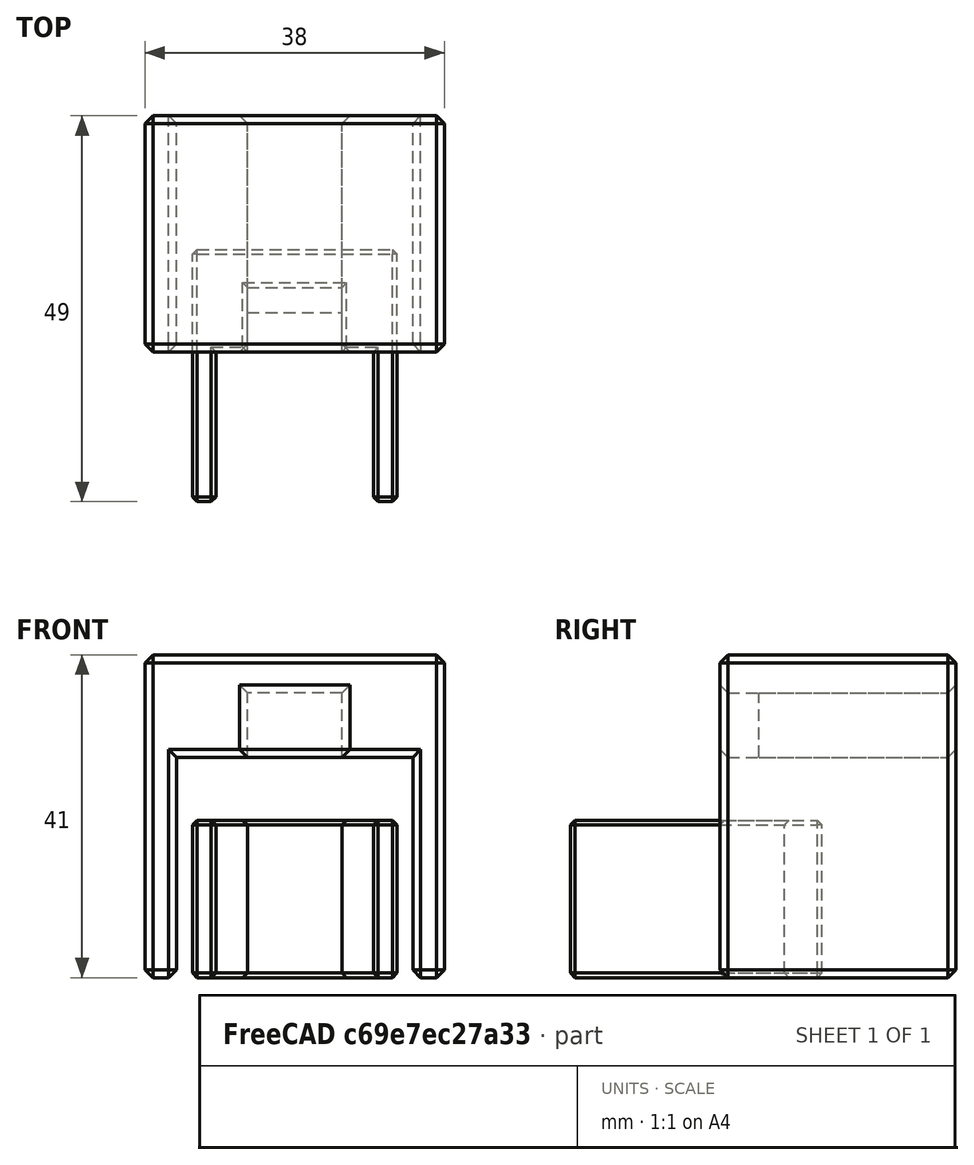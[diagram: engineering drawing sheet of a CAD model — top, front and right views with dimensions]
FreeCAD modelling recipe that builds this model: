
FCSTD DOCUMENT  (FreeCAD 0.18R16146 (Git))
Label: rail-aliner
License: All rights reserved
LicenseURL: http://en.wikipedia.org/wiki/All_rights_reserved
objects: Part::Box×7, Part::MultiFuse×3, Part::Chamfer×3, Part::Cut×2, Part::Feature×1
note: 16 computed .brp shape members not serialized (recipe doc carries the construction recipe); baked Part::Feature solids carry a one-line shape summary decoded from their .brp

FEATURE [Part::Box] Box003  label="Cube003"
  AttacherType = Attacher::AttachEngine3D
  Height = 10.2
  Length = 14.2
  Placement = pos=(-7.1,0,28) rot=(0,0,1;0rad)
  Width = 5
FEATURE [Part::Box] Box005  label="Cube005"
  AttacherType = Attacher::AttachEngine3D
  Height = 28
  Length = 30
  Placement = pos=(-15,0,0) rot=(0,0,1;0rad)
  Width = 30
FEATURE [Part::Box] Box006  label="Cube006"
  AttacherType = Attacher::AttachEngine3D
  Height = 8.2
  Length = 12
  Placement = pos=(-6,0,28) rot=(0,0,1;0rad)
  Width = 30
FEATURE [Part::Box] Box007  label="Cube007"
  AttacherType = Attacher::AttachEngine3D
  Height = 41
  Length = 38
  Placement = pos=(-19,0,0) rot=(0,0,1;0rad)
  Width = 30
FEATURE [Part::Box] Box  label="Cube"
  AttacherType = Attacher::AttachEngine3D
  Height = 20
  Length = 12
  Placement = pos=(-6,0,0) rot=(0,0,1;0rad)
  Width = 8.2
FEATURE [Part::Box] Box008  label="Cube008"
  AttacherType = Attacher::AttachEngine3D
  Height = 20
  Length = 20
  Placement = pos=(-10,-20,0) rot=(0,0,1;0rad)
  Width = 20
FEATURE [Part::Box] Box009  label="Cube009"
  AttacherType = Attacher::AttachEngine3D
  Height = 20
  Length = 26
  Placement = pos=(-13,-19,0) rot=(0,0,1;0rad)
  Width = 32
FEATURE [Part::MultiFuse] Fusion002
  Shapes = -> [Box,Box008]
FEATURE [Part::Cut] Cut003
  Base = -> Box009
  Tool = -> Fusion002
FEATURE [Part::Chamfer] Chamfer002  label="2020"
  Base = -> Cut003
  Edges = 30 edges r=0.6: [Edge1,Edge2,Edge3,Edge4,Edge5,Edge6,Edge7,Edge8,Edge9,Edge10,Edge11,Edge12,Edge13,Edge14,Edge15,Edge16,Edge17,Edge18,Edge19,Edge20,Edge21,Edge22,Edge23,Edge24,Edge25,Edge26,Edge27,Edge28,Edge30,Edge31]
FEATURE [Part::MultiFuse] Fusion
  Shapes = -> [Box006,Box005]
FEATURE [Part::Cut] Cut
  Base = -> Box007
  Tool = -> Fusion
FEATURE [Part::Feature] Cut004
  shape: bbox 38 x 30 x 41 mm, 14 faces (baked)
FEATURE [Part::MultiFuse] Fusion003
  Shapes = -> [Cut,Box003]
FEATURE [Part::Chamfer] Chamfer  label="3030-5mm-spc"
  Base = -> Fusion003
  Edges = 30 edges r=1: [Edge1,Edge5,Edge12,Edge16,Edge17,Edge18,Edge19,Edge20,Edge21,Edge22,Edge23,Edge24,Edge26,Edge29,Edge32,Edge33,Edge34,Edge35,Edge36,Edge37,Edge38,Edge39,Edge40,Edge41,Edge42,Edge43,Edge44,Edge48,Edge49,Edge50]
FEATURE [Part::Chamfer] Chamfer003  label="3030-spc"
  Base = -> Cut004
  Edges = 30 edges r=1: [Edge1,Edge2,Edge3,Edge4,Edge5,Edge6,Edge7,Edge8,Edge9,Edge10,Edge11,Edge12,Edge13,Edge14,Edge15,Edge16,Edge17,Edge18,Edge19,Edge20,Edge21,Edge22,Edge23,Edge24,Edge25,Edge26,Edge27,Edge28,Edge35,Edge36]
